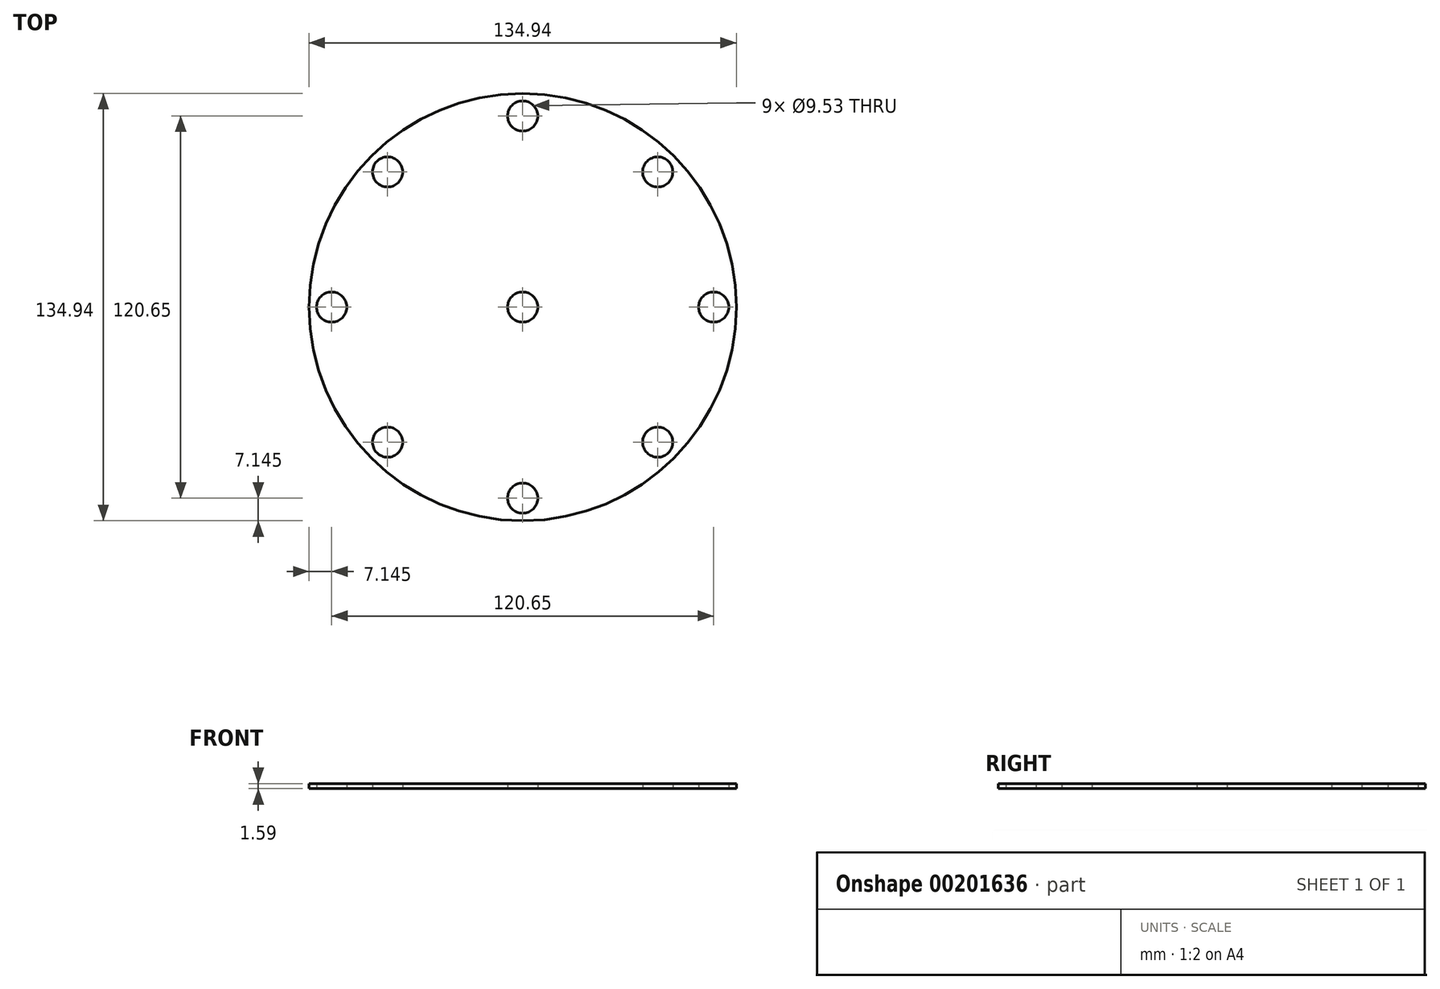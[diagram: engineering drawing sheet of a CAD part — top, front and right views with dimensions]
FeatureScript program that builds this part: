
annotation { "Feature Type Name" : "Feature", "Feature Type Description" : "" }
export const myFeature = defineFeature(function(context is Context, id is Id, definition is map)
    precondition{}
    {
        {
            var Q0;
            Q0=qCreatedBy(makeId("Top.planeOp"),FACE);
            var sketch = newSketch(context, id + "F0", { "sketchPlane" : qUnion([Q0])});
            skCircle(sketch, "E0", {"center": v(0, 0) * mm, "radius": 67.47 * mm});
            skCircle(sketch, "E1", {"center": v(0, 0) * mm, "radius": 4.76 * mm});
            skCircle(sketch, "E2", {"center": v(0, 60.33) * mm, "radius": 4.76 * mm});
            skLineSegment(sketch, "E3.anchor1", {"start": v(0, 0) * mm, "end": v(0, 60.33) * mm, "construction": true});
            skLineSegment(sketch, "E3.anchor2", {"start": v(0, 0) * mm, "end": v(0, 60.33) * mm, "construction": true});
            skCircle(sketch, "E4.1.0", {"center": v(-42.66, 42.66) * mm, "radius": 4.76 * mm});
            skCircle(sketch, "E4.2.0", {"center": v(-60.33, 0) * mm, "radius": 4.76 * mm});
            skCircle(sketch, "E5.1.3.0", {"center": v(-42.66, -42.66) * mm, "radius": 4.76 * mm});
            skCircle(sketch, "E5.1.4.0", {"center": v(0, -60.33) * mm, "radius": 4.76 * mm});
            skCircle(sketch, "E5.1.5.0", {"center": v(42.66, -42.66) * mm, "radius": 4.76 * mm});
            skCircle(sketch, "E5.1.6.0", {"center": v(60.33, 0) * mm, "radius": 4.76 * mm});
            skCircle(sketch, "E5.1.7.0", {"center": v(42.66, 42.66) * mm, "radius": 4.76 * mm});
            skSolve(sketch);
        }
        {
            var Q0;
            Q0=makeQuery(id+"F0.imprint","IMPRINT",FACE,{"disambiguationData":[TD([[makeQuery(id+"F0.imprint","IMPRINT",EDGE,{"derivedFrom":sQuery(id+"F0.wireOp",EDGE,"E0")}),1.0]])]});
            extrude(context, id + "F1", {"entities" : qUnion([Q0]), "depth" : 1.59 * mm});
        }
    });
